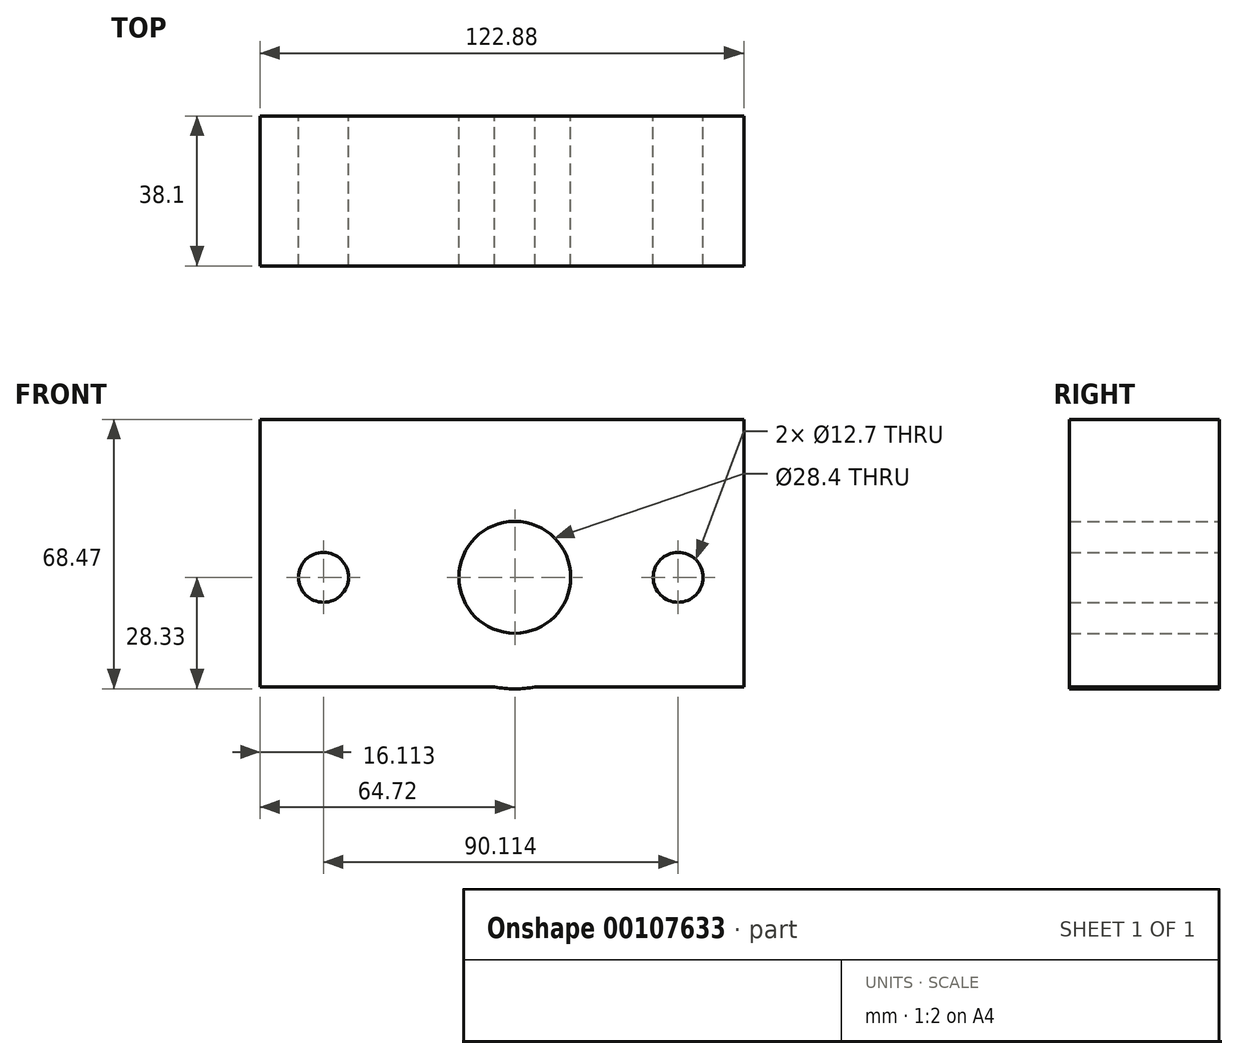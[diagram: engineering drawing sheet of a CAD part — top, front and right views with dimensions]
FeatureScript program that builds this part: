
annotation { "Feature Type Name" : "Feature", "Feature Type Description" : "" }
export const myFeature = defineFeature(function(context is Context, id is Id, definition is map)
    precondition{}
    {
        {
            var Q0;
            Q0=qCreatedBy(makeId("Front.planeOp"),FACE);
            var sketch = newSketch(context, id + "F0", { "sketchPlane" : qUnion([Q0])});
            skCircle(sketch, "E0", {"center": v(0, 0) * mm, "radius": 28.33 * mm});
            skCircle(sketch, "E1", {"center": v(0, 0) * mm, "radius": 14.2 * mm});
            skLineSegment(sketch, "E2.bottom", {"start": v(58.16, -27.85) * mm, "end": v(-64.72, -27.85) * mm});
            skLineSegment(sketch, "E2.top", {"start": v(58.16, 40.14) * mm, "end": v(-64.72, 40.14) * mm});
            skLineSegment(sketch, "E2.left", {"start": v(58.16, -27.85) * mm, "end": v(58.16, 40.14) * mm});
            skLineSegment(sketch, "E2.right", {"start": v(-64.72, -27.85) * mm, "end": v(-64.72, 40.14) * mm});
            skCircle(sketch, "E3", {"center": v(-48.6, 0) * mm, "radius": 6.35 * mm});
            skCircle(sketch, "E4", {"center": v(41.5, 0) * mm, "radius": 6.35 * mm});
            skSolve(sketch);
        }
        {
            var Q0;
            Q0=sQuery(id+"F0.wireOp",EDGE,"E0");
            extrude(context, id + "F1", {"bodyType" : ToolBodyType.SURFACE, "surfaceEntities" : qUnion([Q0]), "depth" : 38.1 * mm});
        }
        {
            var Q0;
            Q0 = qSketchRegion(id + "F0", true);
            extrude(context, id + "F2", {"entities" : qUnion([Q0]), "depth" : 12.7 * mm});
        }
        {
            var Q0;
            Q0=makeQuery(id+"F2.opExtrude","CAP_FACE",FACE,{"disambiguationData":[OSD([sQuery(id+"F0.wireOp",EDGE,"E0"),sQuery(id+"F0.wireOp",EDGE,"E1"),sQuery(id+"F0.wireOp",EDGE,"E2.bottom"),sQuery(id+"F0.wireOp",EDGE,"E2.top"),sQuery(id+"F0.wireOp",EDGE,"E2.left"),sQuery(id+"F0.wireOp",EDGE,"E2.right"),sQuery(id+"F0.wireOp",EDGE,"E3"),sQuery(id+"F0.wireOp",EDGE,"E4")])],"isStart":false});
            extrude(context, id + "F3", {"entities" : qUnion([Q0]), "operationType" : NewBodyOperationType.ADD, "depth" : 25.4 * mm});
        }
    });
